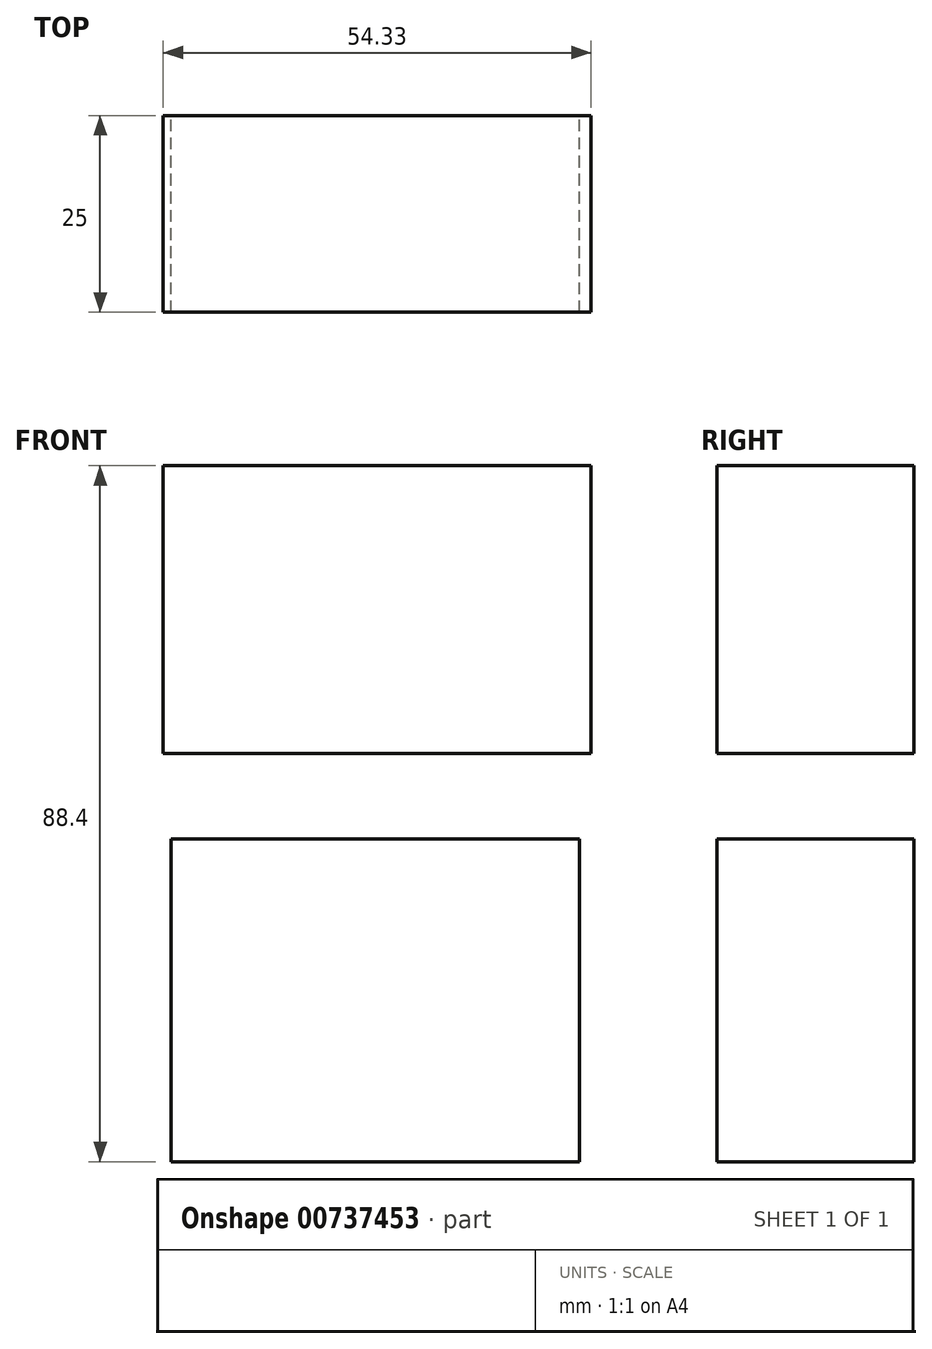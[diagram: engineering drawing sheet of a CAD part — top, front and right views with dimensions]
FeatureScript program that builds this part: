
annotation { "Feature Type Name" : "Feature", "Feature Type Description" : "" }
export const myFeature = defineFeature(function(context is Context, id is Id, definition is map)
    precondition{}
    {
        {
            var Q0;
            Q0=qCreatedBy(makeId("Front.planeOp"),FACE);
            var sketch = newSketch(context, id + "F0", { "sketchPlane" : qUnion([Q0])});
            skLineSegment(sketch, "E0.bottom", {"start": v(-89.02, 19.14) * mm, "end": v(-34.7, 19.14) * mm});
            skLineSegment(sketch, "E0.top", {"start": v(-89.02, 55.68) * mm, "end": v(-34.7, 55.68) * mm});
            skLineSegment(sketch, "E0.left", {"start": v(-89.02, 19.14) * mm, "end": v(-89.02, 55.68) * mm});
            skLineSegment(sketch, "E0.right", {"start": v(-34.7, 19.14) * mm, "end": v(-34.7, 55.68) * mm});
            skPoint(sketch, "E0.middle", {"position": v(-61.86, 37.41) * mm});
            skLineSegment(sketch, "E1.bottom", {"start": v(-88.03, -32.72) * mm, "end": v(-36.18, -32.72) * mm});
            skLineSegment(sketch, "E1.top", {"start": v(-88.03, 8.27) * mm, "end": v(-36.18, 8.27) * mm});
            skLineSegment(sketch, "E1.left", {"start": v(-88.03, -32.72) * mm, "end": v(-88.03, 8.27) * mm});
            skLineSegment(sketch, "E1.right", {"start": v(-36.18, -32.72) * mm, "end": v(-36.18, 8.27) * mm});
            skPoint(sketch, "E1.middle", {"position": v(-62.1, -12.22) * mm});
            skSolve(sketch);
        }
        {
            var Q0;
            Q0=makeQuery(id+"F0.imprint","IMPRINT",FACE,{"disambiguationData":[TD([[makeQuery(id+"F0.imprint","IMPRINT",EDGE,{"derivedFrom":sQuery(id+"F0.wireOp",EDGE,"E1.bottom")}),1.0]])]});
            var Q1;
            Q1=makeQuery(id+"F0.imprint","IMPRINT",FACE,{"disambiguationData":[TD([[makeQuery(id+"F0.imprint","IMPRINT",EDGE,{"derivedFrom":sQuery(id+"F0.wireOp",EDGE,"E0.bottom")}),1.0]])]});
            extrude(context, id + "F1", {"entities" : qUnion([Q0, Q1]), "depth" : 25 * mm, "offsetDistance" : 25 * mm});
        }
    });
